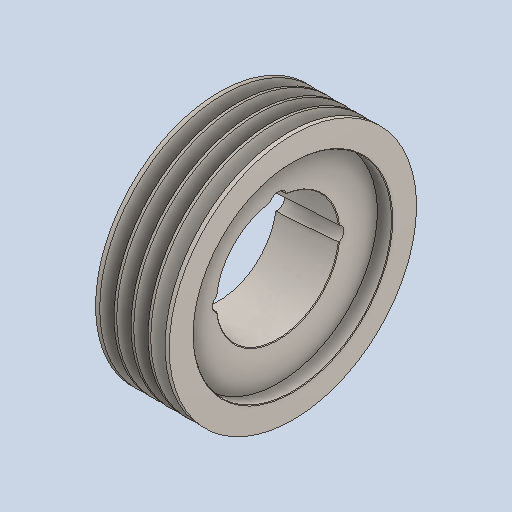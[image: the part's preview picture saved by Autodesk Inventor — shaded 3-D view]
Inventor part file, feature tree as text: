
AUTODESK INVENTOR PART (.ipt)
format: ipt  version: 2024.1 (Build 281209000, 209)  size: 224,256 bytes
history: native  units: in
note: dims shown in document units (in); Inventor stores cm internally (conversion verified against a paired STEP export)
features: chamfer x1
ambient origin geometry x8: Origin, YZ Plane, XZ Plane, XY Plane, X Axis, Y Axis, Z Axis, Center Point
bodies: Solid1 (feature_tree)
feature tree (1):
  chamfer  "Chamfer1"  [1 undecoded]
note: 1 required parameter value undecoded (feature->parameter linkage not recoverable at this tier; creation-order binding heuristic only, values carry confidence <= 0.55)
